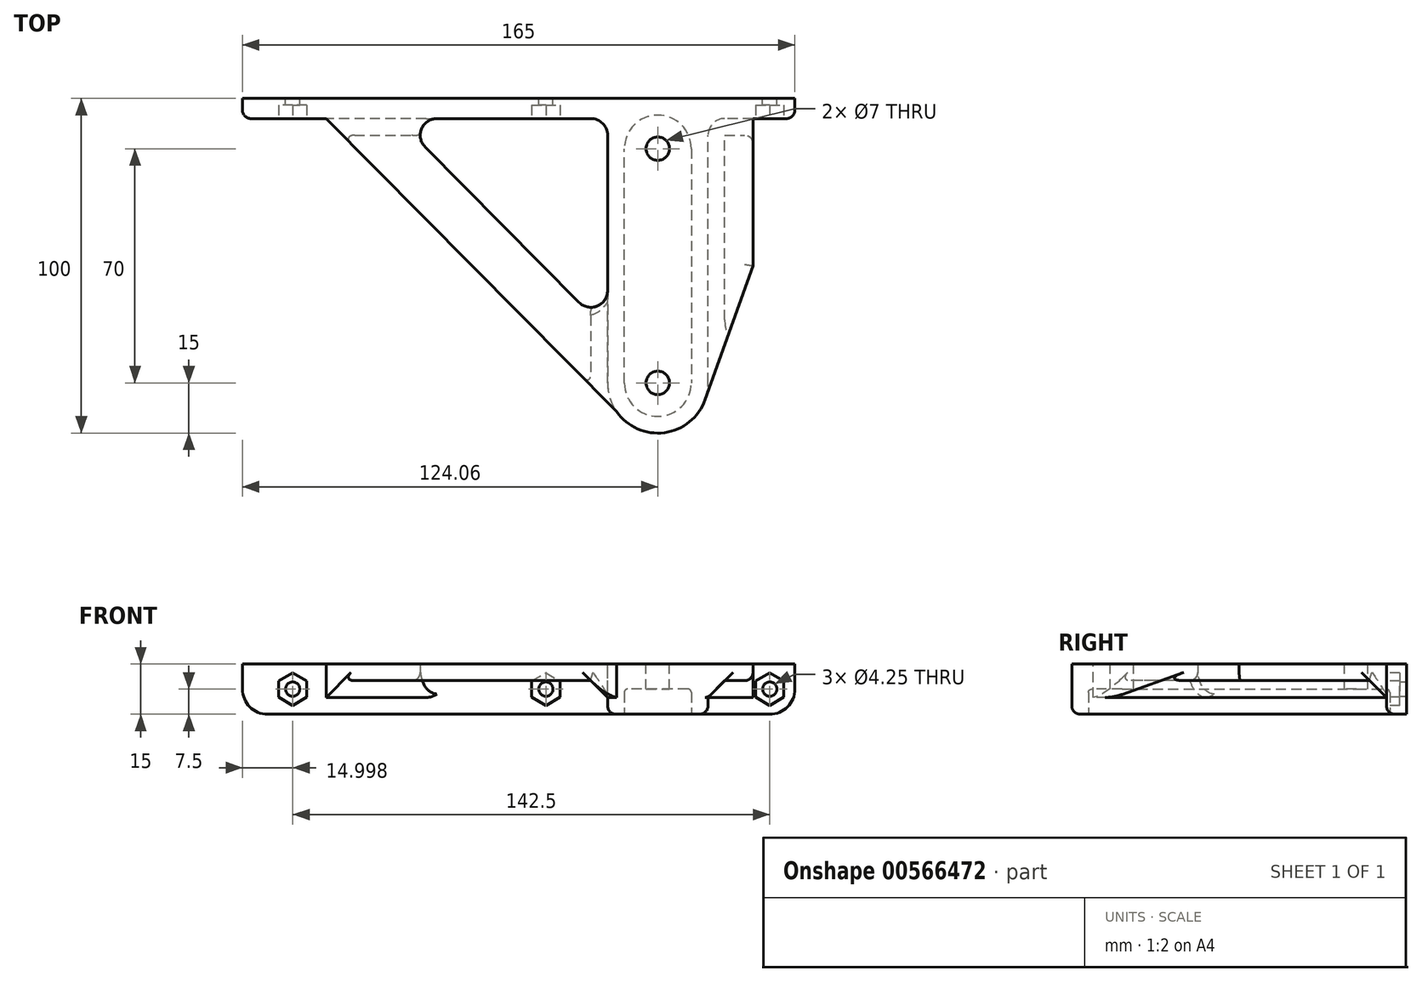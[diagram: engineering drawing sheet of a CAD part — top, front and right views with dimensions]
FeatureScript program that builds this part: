
annotation { "Feature Type Name" : "Feature", "Feature Type Description" : "" }
export const myFeature = defineFeature(function(context is Context, id is Id, definition is map)
    precondition{}
    {
        {
            var Q0;
            Q0=qCreatedBy(makeId("Top.planeOp"),FACE);
            var sketch = newSketch(context, id + "F0", { "sketchPlane" : qUnion([Q0])});
            skLineSegment(sketch, "E0", {"start": v(-124.06, 9) * mm, "end": v(-124.06, 15) * mm});
            skLineSegment(sketch, "E1", {"start": v(-124.06, 15) * mm, "end": v(40.94, 15) * mm});
            skLineSegment(sketch, "E2", {"start": v(40.94, 15) * mm, "end": v(40.94, 9) * mm});
            skLineSegment(sketch, "E3", {"start": v(12.37, -78.48) * mm, "end": v(10, -85) * mm, "construction": true});
            skLineSegment(sketch, "E4", {"start": v(10, -85) * mm, "end": v(-10, -85) * mm, "construction": true});
            skLineSegment(sketch, "E5", {"start": v(-10, -85) * mm, "end": v(-124.06, 0) * mm, "construction": true});
            skCircle(sketch, "E6", {"center": v(0, 0) * mm, "radius": 3.5 * mm});
            skCircle(sketch, "E7", {"center": v(0, -70) * mm, "radius": 3.5 * mm});
            skArc(sketch, "E8", {"start": v(-8.7, -82.22) * mm, "mid": v(4.5, -84.31) * mm, "end": v(14.13, -75.05) * mm});
            skLineSegment(sketch, "E9", {"start": v(28.44, -34.99) * mm, "end": v(14.13, -75.05) * mm});
            skLineSegment(sketch, "E10", {"start": v(-124.06, 0) * mm, "end": v(-8.7, -82.22) * mm, "construction": true});
            skLineSegment(sketch, "E11", {"start": v(-77.95, 9) * mm, "end": v(-15, 9) * mm});
            skLineSegment(sketch, "E12", {"start": v(-15, 9) * mm, "end": v(-15, -54.55) * mm});
            skLineSegment(sketch, "E13", {"start": v(-15, -54.55) * mm, "end": v(-77.95, 9) * mm});
            skLineSegment(sketch, "E14", {"start": v(-124.06, 9) * mm, "end": v(-99.06, 9) * mm});
            skLineSegment(sketch, "E15", {"start": v(-99.06, 9) * mm, "end": v(-8.7, -82.22) * mm});
            skLineSegment(sketch, "E16", {"start": v(28.44, 9) * mm, "end": v(40.94, 9) * mm});
            skLineSegment(sketch, "E17", {"start": v(28.44, 9) * mm, "end": v(28.44, -34.99) * mm});
            skPoint(sketch, "E18.orphan", {"position": v(40.94, 0) * mm});
            skSolve(sketch);
        }
        {
            var Q0;
            Q0=qSketchRegion(id+"F0",true);
            extrude(context, id + "F1", {"entities" : qUnion([Q0]), "oppositeDirection" : true, "depth" : 5 * mm, "offsetDistance" : 25 * mm});
        }
        {
            var Q0;
            Q0=makeQuery(id+"F1.opExtrude","CAP_FACE",FACE,{"disambiguationData":[OSD([sQuery(id+"F0.wireOp",EDGE,"E0"),sQuery(id+"F0.wireOp",EDGE,"E1"),sQuery(id+"F0.wireOp",EDGE,"E2"),sQuery(id+"F0.wireOp",EDGE,"E6"),sQuery(id+"F0.wireOp",EDGE,"E7"),sQuery(id+"F0.wireOp",EDGE,"E8"),sQuery(id+"F0.wireOp",EDGE,"E9"),sQuery(id+"F0.wireOp",EDGE,"E11"),sQuery(id+"F0.wireOp",EDGE,"E12"),sQuery(id+"F0.wireOp",EDGE,"E13"),sQuery(id+"F0.wireOp",EDGE,"E14"),sQuery(id+"F0.wireOp",EDGE,"E15"),sQuery(id+"F0.wireOp",EDGE,"E16"),sQuery(id+"F0.wireOp",EDGE,"E17")])],"isStart":true});
            var sketch = newSketch(context, id + "F2", { "sketchPlane" : qUnion([Q0])});
            skLineSegment(sketch, "E19.bottom", {"start": v(-124.06, 15) * mm, "end": v(-15, 15) * mm});
            skLineSegment(sketch, "E19.top", {"start": v(-124.06, 9) * mm, "end": v(-15, 9) * mm});
            skLineSegment(sketch, "E19.left", {"start": v(-124.06, 15) * mm, "end": v(-124.06, 9) * mm});
            skLineSegment(sketch, "E19.right", {"start": v(40.94, 15) * mm, "end": v(40.94, 9) * mm});
            skLineSegment(sketch, "E20.left", {"start": v(-15, -70) * mm, "end": v(-15, 9) * mm});
            skLineSegment(sketch, "E20.right", {"start": v(15, -70) * mm, "end": v(15, 9) * mm});
            skLineSegment(sketch, "E21.trimOffspring", {"start": v(15, 9) * mm, "end": v(40.94, 9) * mm});
            skCircle(sketch, "E22", {"center": v(0, 0) * mm, "radius": 3.5 * mm});
            skCircle(sketch, "E23", {"center": v(0, -70) * mm, "radius": 3.5 * mm});
            skArc(sketch, "E24", {"start": v(0, -85) * mm, "mid": v(10.6, -80.6) * mm, "end": v(15, -70) * mm});
            skArc(sketch, "E25.MirrorCS", {"start": v(0, -85) * mm, "mid": v(-10.6, -80.6) * mm, "end": v(-15, -70) * mm});
            skLineSegment(sketch, "E26", {"start": v(0, -70) * mm, "end": v(15, -70) * mm, "construction": true});
            skLineSegment(sketch, "E27.trimOffspring", {"start": v(15, 15) * mm, "end": v(40.94, 15) * mm});
            skPoint(sketch, "E28.orphan", {"position": v(0, -55) * mm});
            skPoint(sketch, "E29.trimOffspring.end.orphan", {"position": v(-15, -70) * mm});
            skPoint(sketch, "E30.orphan", {"position": v(15, -70) * mm});
            skLineSegment(sketch, "E31", {"start": v(-15, 15) * mm, "end": v(15, 15) * mm});
            skSolve(sketch);
        }
        {
            var Q0;
            Q0=qSketchRegion(id+"F2",true);
            extrude(context, id + "F3", {"entities" : qUnion([Q0]), "operationType" : NewBodyOperationType.ADD, "oppositeDirection" : true, "depth" : 15 * mm, "offsetDistance" : 25 * mm});
        }
        {
            var Q0;
            Q0=makeQuery(id+"F3.opExtrude","SWEPT_EDGE",EDGE,{"disambiguationData":[OSD([sQuery(id+"F2.wireOp",EDGE,"E19.top"),sQuery(id+"F2.wireOp",EDGE,"E20.left")])]});
            var Q1;
            Q1=makeQuery(id+"F3.opExtrude","SWEPT_EDGE",EDGE,{"disambiguationData":[OSD([sQuery(id+"F2.wireOp",EDGE,"E20.right"),sQuery(id+"F2.wireOp",EDGE,"E21.trimOffspring")])]});
            fillet(context, id + "F4", {"entities" : qUnion([Q0, Q1]), "radius" : 5 * mm, "tangentPropagation" : true, "allowEdgeOverflow" : false});
        }
        {
            var Q0;
            Q0=makeQuery(id+"F3.boolean.opBoolean","MERGE",FACE,{"derivedFrom":[makeQuery(id+"F1.opExtrude","SWEPT_FACE",FACE,{"disambiguationData":[OSD([sQuery(id+"F0.wireOp",EDGE,"E1")])]}),makeQuery(id+"F3.opExtrude","SWEPT_FACE",FACE,{"disambiguationData":[OSD([sQuery(id+"F2.wireOp",EDGE,"E19.bottom")])]})]});
            var sketch = newSketch(context, id + "F5", { "sketchPlane" : qUnion([Q0])});
            skCircle(sketch, "E32", {"center": v(-33.44, -7.5) * mm, "radius": 2.12 * mm});
            skCircle(sketch, "E33", {"center": v(109.06, -7.5) * mm, "radius": 2.12 * mm});
            skCircle(sketch, "E34.MirrorC", {"center": v(33.44, -7.5) * mm, "radius": 2.12 * mm});
            skSolve(sketch);
        }
        {
            var Q0;
            Q0=qSketchRegion(id+"F5",true);
            extrude(context, id + "F6", {"entities" : qUnion([Q0]), "operationType" : NewBodyOperationType.REMOVE, "oppositeDirection" : true, "depth" : 25 * mm});
        }
        {
            var Q0;
            {var subQ0=sQuery(id+"F0.wireOp",EDGE,"E8");var subQ1=sQuery(id+"F0.wireOp",EDGE,"E9");var subQ2=sQuery(id+"F0.wireOp",EDGE,"brWuAORZ-QQ3N-mHyy-jjcm-9xjy5NoIPpaN");var subQ3=sQuery(id+"F0.wireOp",EDGE,"E2");var subQ4=sQuery(id+"F2.wireOp",EDGE,"E20.right");var subQ5=sQuery(id+"F2.wireOp",EDGE,"E21.trimOffspring");Q0=makeQuery(id+"F4.opFillet","BLEND_EDGE",EDGE,{"blendedFrom":[makeQuery(id+"F3.opExtrude","SWEPT_EDGE",EDGE,{"disambiguationData":[OSD([subQ4,subQ5])]}),makeQuery(id+"F3.boolean.opBoolean","SPLIT",FACE,{"disambiguationData":[TD([makeQuery(id+"F1.opExtrude","SWEPT_FACE",FACE,{"disambiguationData":[OSD([subQ3])]})])],"derivedFrom":makeQuery(id+"F1.opExtrude","CAP_FACE",FACE,{"disambiguationData":[OSD([sQuery(id+"F0.wireOp",EDGE,"E0"),sQuery(id+"F0.wireOp",EDGE,"E1"),subQ3,sQuery(id+"F0.wireOp",EDGE,"E6"),sQuery(id+"F0.wireOp",EDGE,"E7"),subQ2,sQuery(id+"F0.wireOp",EDGE,"hGYEL4FP-7Z2F-9BLv-NZoW-4O7jBzdm4NG0"),sQuery(id+"F0.wireOp",EDGE,"Ev3Ag6zw-3mFU-VTcE-mw61-bQwCWqHxOj75"),sQuery(id+"F0.wireOp",EDGE,"rvlW2tZY-N1AQ-Yf2F-EbRQ-ggfH0PUhPHp1"),subQ0,subQ1,sQuery(id+"F0.wireOp",EDGE,"E10")])],"isStart":false})})],"blendedInto":[makeQuery(id+"F3.boolean.opBoolean","SPLIT",FACE,{"disambiguationData":[TD([makeQuery(id+"F1.opExtrude","SWEPT_FACE",FACE,{"disambiguationData":[OSD([subQ3])]})])],"derivedFrom":makeQuery(id+"F1.opExtrude","CAP_FACE",FACE,{"disambiguationData":[OSD([sQuery(id+"F0.wireOp",EDGE,"E0"),sQuery(id+"F0.wireOp",EDGE,"E1"),subQ3,sQuery(id+"F0.wireOp",EDGE,"E6"),sQuery(id+"F0.wireOp",EDGE,"E7"),subQ2,sQuery(id+"F0.wireOp",EDGE,"hGYEL4FP-7Z2F-9BLv-NZoW-4O7jBzdm4NG0"),sQuery(id+"F0.wireOp",EDGE,"Ev3Ag6zw-3mFU-VTcE-mw61-bQwCWqHxOj75"),sQuery(id+"F0.wireOp",EDGE,"rvlW2tZY-N1AQ-Yf2F-EbRQ-ggfH0PUhPHp1"),subQ0,subQ1,sQuery(id+"F0.wireOp",EDGE,"E10")])],"isStart":false})})]});}
            var Q1;
            Q1=makeQuery(id+"F3.opExtrude","CAP_EDGE",EDGE,{"disambiguationData":[OSD([sQuery(id+"F2.wireOp",EDGE,"E20.left")])],"isStart":true});
            var Q2;
            Q2=makeQuery(id+"F3.opExtrude","CAP_EDGE",EDGE,{"disambiguationData":[OSD([sQuery(id+"F2.wireOp",EDGE,"E19.top")])],"isStart":true});
            var Q3;
            Q3=makeQuery(id+"F3.opExtrude","CAP_EDGE",EDGE,{"disambiguationData":[OSD([sQuery(id+"F2.wireOp",EDGE,"E21.trimOffspring")])],"isStart":true});
            var Q4;
            Q4=makeQuery(id+"F3.boolean.opBoolean","INTERSECT",EDGE,{"derivedFrom":[makeQuery(id+"F1.opExtrude","CAP_FACE",FACE,{"disambiguationData":[OSD([sQuery(id+"F0.wireOp",EDGE,"E0"),sQuery(id+"F0.wireOp",EDGE,"E1"),sQuery(id+"F0.wireOp",EDGE,"E2"),sQuery(id+"F0.wireOp",EDGE,"E6"),sQuery(id+"F0.wireOp",EDGE,"E7"),sQuery(id+"F0.wireOp",EDGE,"E8"),sQuery(id+"F0.wireOp",EDGE,"E9"),sQuery(id+"F0.wireOp",EDGE,"E11"),sQuery(id+"F0.wireOp",EDGE,"E12"),sQuery(id+"F0.wireOp",EDGE,"E13"),sQuery(id+"F0.wireOp",EDGE,"E14"),sQuery(id+"F0.wireOp",EDGE,"E15"),sQuery(id+"F0.wireOp",EDGE,"E16"),sQuery(id+"F0.wireOp",EDGE,"E17")])],"isStart":false}),makeQuery(id+"F3.opExtrude","SWEPT_FACE",FACE,{"disambiguationData":[OSD([sQuery(id+"F2.wireOp",EDGE,"E19.top")])]})]});
            var Q5;
            Q5=makeQuery(id+"F3.boolean.opBoolean","INTERSECT",EDGE,{"derivedFrom":[makeQuery(id+"F1.opExtrude","CAP_FACE",FACE,{"disambiguationData":[OSD([sQuery(id+"F0.wireOp",EDGE,"E0"),sQuery(id+"F0.wireOp",EDGE,"E1"),sQuery(id+"F0.wireOp",EDGE,"E2"),sQuery(id+"F0.wireOp",EDGE,"E6"),sQuery(id+"F0.wireOp",EDGE,"E7"),sQuery(id+"F0.wireOp",EDGE,"E8"),sQuery(id+"F0.wireOp",EDGE,"E9"),sQuery(id+"F0.wireOp",EDGE,"E11"),sQuery(id+"F0.wireOp",EDGE,"E12"),sQuery(id+"F0.wireOp",EDGE,"E13"),sQuery(id+"F0.wireOp",EDGE,"E14"),sQuery(id+"F0.wireOp",EDGE,"E15"),sQuery(id+"F0.wireOp",EDGE,"E16"),sQuery(id+"F0.wireOp",EDGE,"E17")])],"isStart":false}),makeQuery(id+"F3.opExtrude","SWEPT_FACE",FACE,{"disambiguationData":[OSD([sQuery(id+"F2.wireOp",EDGE,"E20.left")])]})]});
            var Q6;
            Q6=makeQuery(id+"F3.boolean.opBoolean","INTERSECT",EDGE,{"derivedFrom":[makeQuery(id+"F1.opExtrude","CAP_FACE",FACE,{"disambiguationData":[OSD([sQuery(id+"F0.wireOp",EDGE,"E0"),sQuery(id+"F0.wireOp",EDGE,"E1"),sQuery(id+"F0.wireOp",EDGE,"E2"),sQuery(id+"F0.wireOp",EDGE,"E6"),sQuery(id+"F0.wireOp",EDGE,"E7"),sQuery(id+"F0.wireOp",EDGE,"E8"),sQuery(id+"F0.wireOp",EDGE,"E9"),sQuery(id+"F0.wireOp",EDGE,"E11"),sQuery(id+"F0.wireOp",EDGE,"E12"),sQuery(id+"F0.wireOp",EDGE,"E13"),sQuery(id+"F0.wireOp",EDGE,"E14"),sQuery(id+"F0.wireOp",EDGE,"E15"),sQuery(id+"F0.wireOp",EDGE,"E16"),sQuery(id+"F0.wireOp",EDGE,"E17")])],"isStart":false}),makeQuery(id+"F3.opExtrude","SWEPT_FACE",FACE,{"disambiguationData":[OSD([sQuery(id+"F2.wireOp",EDGE,"E20.right")])]})]});
            chamfer(context, id + "F7", {"entities" : qUnion([Q0, Q1, Q2, Q3, Q4, Q5, Q6]), "width" : 5 * mm, "tangentPropagation" : true});
        }
        {
            var Q0;
            Q0=makeQuery(id+"F1.opExtrude","SWEPT_EDGE",EDGE,{"disambiguationData":[OSD([sQuery(id+"F0.wireOp",EDGE,"E12"),sQuery(id+"F0.wireOp",EDGE,"E13")])]});
            var Q1;
            Q1=makeQuery(id+"F1.opExtrude","SWEPT_EDGE",EDGE,{"disambiguationData":[OSD([sQuery(id+"F0.wireOp",EDGE,"E11"),sQuery(id+"F0.wireOp",EDGE,"E12")])]});
            var Q2;
            Q2=makeQuery(id+"F1.opExtrude","SWEPT_EDGE",EDGE,{"disambiguationData":[OSD([sQuery(id+"F0.wireOp",EDGE,"E11"),sQuery(id+"F0.wireOp",EDGE,"E13")])]});
            fillet(context, id + "F8", {"entities" : qUnion([Q0, Q1, Q2]), "radius" : 5 * mm, "tangentPropagation" : true, "allowEdgeOverflow" : false});
        }
        {
            var Q0;
            Q0=makeQuery(id+"F3.opExtrude","CAP_FACE",FACE,{"disambiguationData":[OSD([sQuery(id+"F2.wireOp",EDGE,"E19.bottom"),sQuery(id+"F2.wireOp",EDGE,"E19.top"),sQuery(id+"F2.wireOp",EDGE,"E19.left"),sQuery(id+"F2.wireOp",EDGE,"E19.right"),sQuery(id+"F2.wireOp",EDGE,"E20.left"),sQuery(id+"F2.wireOp",EDGE,"E20.right"),sQuery(id+"F2.wireOp",EDGE,"E21.trimOffspring"),sQuery(id+"F2.wireOp",EDGE,"E22"),sQuery(id+"F2.wireOp",EDGE,"E23"),sQuery(id+"F2.wireOp",EDGE,"E24"),sQuery(id+"F2.wireOp",EDGE,"E25.MirrorCS")])],"isStart":false});
            var sketch = newSketch(context, id + "F9", { "sketchPlane" : qUnion([Q0])});
            skLineSegment(sketch, "E35.bottom", {"start": v(10, 0) * mm, "end": v(10, 0) * mm});
            skLineSegment(sketch, "E35.top", {"start": v(-10, 70) * mm, "end": v(-10, 0) * mm});
            skLineSegment(sketch, "E35.left", {"start": v(10, 0) * mm, "end": v(10, 70) * mm});
            skLineSegment(sketch, "E35.right", {"start": v(-10, 0) * mm, "end": v(-10, 0) * mm});
            skPoint(sketch, "E35.middle", {"position": v(0, -35) * mm});
            skArc(sketch, "E36.filletArc", {"start": v(-10, 0) * mm, "mid": v(0, -10) * mm, "end": v(10, 0) * mm});
            skArc(sketch, "E37.filletArc", {"start": v(10, 70) * mm, "mid": v(0, 80) * mm, "end": v(-10, 70) * mm});
            skPoint(sketch, "E38.visualSharp", {"position": v(10, 0.04) * mm});
            skSolve(sketch);
        }
        {
            var Q0;
            Q0=qSketchRegion(id+"F9",true);
            extrude(context, id + "F10", {"entities" : qUnion([Q0]), "operationType" : NewBodyOperationType.REMOVE, "oppositeDirection" : true, "depth" : 7.5 * mm});
        }
        {
            var Q0;
            Q0=makeQuery(id+"F3.opExtrude","CAP_EDGE",EDGE,{"disambiguationData":[OSD([sQuery(id+"F2.wireOp",EDGE,"E19.right")])],"isStart":false});
            var Q1;
            Q1=makeQuery(id+"F3.opExtrude","CAP_EDGE",EDGE,{"disambiguationData":[OSD([sQuery(id+"F2.wireOp",EDGE,"E19.left")])],"isStart":false});
            fillet(context, id + "F11", {"entities" : qUnion([Q0, Q1]), "radius" : 7.5 * mm, "tangentPropagation" : true, "allowEdgeOverflow" : false});
        }
        {
            var Q0;
            Q0=makeQuery(id+"F3.opExtrude","CAP_EDGE",EDGE,{"disambiguationData":[OSD([sQuery(id+"F2.wireOp",EDGE,"E20.left")])],"isStart":false});
            var Q1;
            Q1=makeQuery(id+"F10.boolean.opBoolean","COPY",EDGE,{"derivedFrom":makeQuery(id+"F10.opExtrude","CAP_EDGE",EDGE,{"disambiguationData":[OSD([sQuery(id+"F9.wireOp",EDGE,"E36.filletArc"),sQuery(id+"F9.wireOp",EDGE,"E37.filletArc")])],"isStart":true})});
            var Q2;
            Q2=makeQuery(id+"F7.opChamfer","BLEND_EDGE",EDGE,{"blendedFrom":[makeQuery(id+"F3.opExtrude","CAP_EDGE",EDGE,{"disambiguationData":[OSD([sQuery(id+"F2.wireOp",EDGE,"E19.top")])],"isStart":true}),makeQuery(id+"F1.opExtrude","SWEPT_FACE",FACE,{"disambiguationData":[OSD([sQuery(id+"F0.wireOp",EDGE,"E15")])]})],"blendedInto":[makeQuery(id+"F1.opExtrude","SWEPT_FACE",FACE,{"disambiguationData":[OSD([sQuery(id+"F0.wireOp",EDGE,"E15")])]})]});
            var Q3;
            Q3=makeQuery(id+"F8.opFillet","BLEND_EDGE",EDGE,{"blendedFrom":[makeQuery(id+"F1.opExtrude","SWEPT_EDGE",EDGE,{"disambiguationData":[OSD([sQuery(id+"F0.wireOp",EDGE,"E11"),sQuery(id+"F0.wireOp",EDGE,"E13")])]}),makeQuery(id+"F7.opChamfer","BLEND_FACE",FACE,{"disambiguationData":[OSD([sQuery(id+"F2.wireOp",EDGE,"E19.top")])]})],"blendedInto":[makeQuery(id+"F7.opChamfer","BLEND_FACE",FACE,{"disambiguationData":[OSD([sQuery(id+"F2.wireOp",EDGE,"E19.top")])]})]});
            var Q4;
            Q4=makeQuery(id+"F7.opChamfer","BLEND_EDGE",EDGE,{"blendedFrom":[makeQuery(id+"F3.opExtrude","CAP_EDGE",EDGE,{"disambiguationData":[OSD([sQuery(id+"F2.wireOp",EDGE,"E21.trimOffspring")])],"isStart":true}),makeQuery(id+"F1.opExtrude","SWEPT_FACE",FACE,{"disambiguationData":[OSD([sQuery(id+"F0.wireOp",EDGE,"E17")])]})],"blendedInto":[makeQuery(id+"F1.opExtrude","SWEPT_FACE",FACE,{"disambiguationData":[OSD([sQuery(id+"F0.wireOp",EDGE,"E17")])]})]});
            var Q5;
            {var subQ0=sQuery(id+"F0.wireOp",EDGE,"E15");var subQ1=makeQuery(id+"F1.opExtrude","SWEPT_FACE",FACE,{"disambiguationData":[OSD([subQ0])]});var subQ2=sQuery(id+"F0.wireOp",EDGE,"E12");var subQ3=sQuery(id+"F0.wireOp",EDGE,"E8");var subQ4=makeQuery(id+"F1.opExtrude","CAP_FACE",FACE,{"disambiguationData":[OSD([sQuery(id+"F0.wireOp",EDGE,"E0"),sQuery(id+"F0.wireOp",EDGE,"E1"),sQuery(id+"F0.wireOp",EDGE,"E2"),sQuery(id+"F0.wireOp",EDGE,"E6"),sQuery(id+"F0.wireOp",EDGE,"E7"),subQ3,sQuery(id+"F0.wireOp",EDGE,"E9"),sQuery(id+"F0.wireOp",EDGE,"E11"),subQ2,sQuery(id+"F0.wireOp",EDGE,"E13"),sQuery(id+"F0.wireOp",EDGE,"E14"),subQ0,sQuery(id+"F0.wireOp",EDGE,"E16"),sQuery(id+"F0.wireOp",EDGE,"E17")])],"isStart":false});var subQ5=sQuery(id+"F2.wireOp",EDGE,"E25.MirrorCS");var subQ6=sQuery(id+"F2.wireOp",EDGE,"E24");var subQ8=makeQuery(id+"F1.opExtrude","SWEPT_FACE",FACE,{"disambiguationData":[OSD([subQ3])]});var subQ9=makeQuery(id+"F3.opExtrude","SWEPT_FACE",FACE,{"disambiguationData":[OSD([subQ6,subQ5])]});Q5=makeQuery(id+"F7.opChamfer","BLEND_EDGE",EDGE,{"blendedFrom":[makeQuery(id+"F3.boolean.opBoolean","SPLIT",EDGE,{"disambiguationData":[topologyDisambiguationEdgeConnected([subQ4,subQ8,subQ9]),TD([makeQuery(id+"F1.opExtrude","SWEPT_FACE",FACE,{"disambiguationData":[OSD([subQ2])]})])],"derivedFrom":makeQuery(id+"F3.opExtrude","CAP_EDGE",EDGE,{"disambiguationData":[OSD([subQ6,subQ5])],"isStart":true})}),subQ1],"blendedInto":[subQ1]});}
            var Q6;
            Q6=makeQuery(id+"F8.opFillet","BLEND_EDGE",EDGE,{"blendedFrom":[makeQuery(id+"F1.opExtrude","SWEPT_EDGE",EDGE,{"disambiguationData":[OSD([sQuery(id+"F0.wireOp",EDGE,"E12"),sQuery(id+"F0.wireOp",EDGE,"E13")])]}),makeQuery(id+"F7.opChamfer","BLEND_FACE",FACE,{"disambiguationData":[OSD([sQuery(id+"F2.wireOp",EDGE,"E20.left")])]})],"blendedInto":[makeQuery(id+"F7.opChamfer","BLEND_FACE",FACE,{"disambiguationData":[OSD([sQuery(id+"F2.wireOp",EDGE,"E20.left")])]})]});
            var Q7;
            Q7=makeQuery(id+"F1.opExtrude","CAP_EDGE",EDGE,{"disambiguationData":[OSD([sQuery(id+"F0.wireOp",EDGE,"E15")])],"isStart":false});
            var Q8;
            Q8=makeQuery(id+"F1.opExtrude","CAP_EDGE",EDGE,{"disambiguationData":[OSD([sQuery(id+"F0.wireOp",EDGE,"E17")])],"isStart":false});
            var Q9;
            Q9=makeQuery(id+"F1.opExtrude","CAP_EDGE",EDGE,{"disambiguationData":[OSD([sQuery(id+"F0.wireOp",EDGE,"E9")])],"isStart":false});
            var Q10;
            Q10=makeQuery(id+"F1.opExtrude","CAP_EDGE",EDGE,{"disambiguationData":[OSD([sQuery(id+"F0.wireOp",EDGE,"E13")])],"isStart":false});
            fillet(context, id + "F12", {"entities" : qUnion([Q0, Q1, Q2, Q3, Q4, Q5, Q6, Q7, Q8, Q9, Q10]), "radius" : 2.5 * mm, "tangentPropagation" : true, "allowEdgeOverflow" : false});
        }
        {
            var Q0;
            Q0=makeQuery(id+"F10.boolean.opBoolean","COPY",EDGE,{"derivedFrom":makeQuery(id+"F10.opExtrude","CAP_EDGE",EDGE,{"disambiguationData":[OSD([sQuery(id+"F9.wireOp",EDGE,"E36.filletArc"),sQuery(id+"F9.wireOp",EDGE,"E37.filletArc")])],"isStart":false})});
            fillet(context, id + "F13", {"entities" : qUnion([Q0]), "radius" : 1 * mm, "tangentPropagation" : true, "allowEdgeOverflow" : false});
        }
        {
            var Q0;
            Q0=makeQuery(id+"F3.boolean.opBoolean","MERGE",FACE,{"derivedFrom":[makeQuery(id+"F1.opExtrude","SWEPT_FACE",FACE,{"disambiguationData":[OSD([sQuery(id+"F0.wireOp",EDGE,"E11")])]}),makeQuery(id+"F1.opExtrude","SWEPT_FACE",FACE,{"disambiguationData":[OSD([sQuery(id+"F0.wireOp",EDGE,"E14")])]}),makeQuery(id+"F3.opExtrude","SWEPT_FACE",FACE,{"disambiguationData":[OSD([sQuery(id+"F2.wireOp",EDGE,"E19.top")])]})]});
            var sketch = newSketch(context, id + "F14", { "sketchPlane" : qUnion([Q0])});
            skCircle(sketch, "E39.cCircle", {"center": v(-109.06, -7.5) * mm, "radius": 4.22 * mm, "construction": true});
            skLineSegment(sketch, "E39.0", {"start": v(-113.29, -9.94) * mm, "end": v(-113.29, -5.06) * mm});
            skLineSegment(sketch, "E39.1", {"start": v(-113.29, -5.06) * mm, "end": v(-109.06, -2.62) * mm});
            skLineSegment(sketch, "E39.2", {"start": v(-109.06, -2.62) * mm, "end": v(-104.84, -5.06) * mm});
            skLineSegment(sketch, "E39.3", {"start": v(-104.84, -5.06) * mm, "end": v(-104.84, -9.94) * mm});
            skLineSegment(sketch, "E39.4", {"start": v(-104.84, -9.94) * mm, "end": v(-109.06, -12.38) * mm});
            skLineSegment(sketch, "E39.5", {"start": v(-109.06, -12.38) * mm, "end": v(-113.29, -9.94) * mm});
            skPoint(sketch, "E39.0.midPoint", {"position": v(-113.29, -7.5) * mm});
            skCircle(sketch, "E40.cCircle", {"center": v(-33.44, -7.5) * mm, "radius": 4.22 * mm, "construction": true});
            skLineSegment(sketch, "E40.0", {"start": v(-29.21, -5.06) * mm, "end": v(-29.21, -9.94) * mm});
            skLineSegment(sketch, "E40.1", {"start": v(-29.21, -9.94) * mm, "end": v(-33.44, -12.38) * mm});
            skLineSegment(sketch, "E40.2", {"start": v(-33.44, -12.38) * mm, "end": v(-37.66, -9.94) * mm});
            skLineSegment(sketch, "E40.3", {"start": v(-37.66, -9.94) * mm, "end": v(-37.66, -5.06) * mm});
            skLineSegment(sketch, "E40.4", {"start": v(-37.66, -5.06) * mm, "end": v(-33.44, -2.62) * mm});
            skLineSegment(sketch, "E40.5", {"start": v(-33.44, -2.62) * mm, "end": v(-29.21, -5.06) * mm});
            skPoint(sketch, "E40.0.midPoint", {"position": v(-29.21, -7.5) * mm});
            skCircle(sketch, "E41.cCircle", {"center": v(33.44, -7.5) * mm, "radius": 4.22 * mm, "construction": true});
            skLineSegment(sketch, "E41.0", {"start": v(37.66, -5.06) * mm, "end": v(37.66, -9.94) * mm});
            skLineSegment(sketch, "E41.1", {"start": v(37.66, -9.94) * mm, "end": v(33.44, -12.38) * mm});
            skLineSegment(sketch, "E41.2", {"start": v(33.44, -12.38) * mm, "end": v(29.21, -9.94) * mm});
            skLineSegment(sketch, "E41.3", {"start": v(29.21, -9.94) * mm, "end": v(29.21, -5.06) * mm});
            skLineSegment(sketch, "E41.4", {"start": v(29.21, -5.06) * mm, "end": v(33.44, -2.62) * mm});
            skLineSegment(sketch, "E41.5", {"start": v(33.44, -2.62) * mm, "end": v(37.66, -5.06) * mm});
            skPoint(sketch, "E41.0.midPoint", {"position": v(37.66, -7.5) * mm});
            skSolve(sketch);
        }
        {
            var Q0;
            Q0=qSketchRegion(id+"F14",true);
            extrude(context, id + "F15", {"entities" : qUnion([Q0]), "operationType" : NewBodyOperationType.REMOVE, "oppositeDirection" : true, "depth" : 4 * mm, "offsetDistance" : 25 * mm});
        }
    });
